# Revit family: Building-ConnessioniIEC309-GEWISS-67IB-PRESE-INTERBLOCCATE_IP67_SENZA_FONDO
name_source: partatom
category: Apparecchi elettrici
units: mm (PartAtom-declared; Revit-internal decimal feet)

## family parameters
Condiviso = Sì
Host = Superficie
Mantenere orientamento annotazione = Sì
Punto di calcolo locali = Sì
Quota connettore circolare = Usa diametro
Taglio con vuoti quando caricato = Sì
Tipo di parte = Normale

## types (23) — shared parameters
Catalogo = BUILDING
Catalogo Serie = 67 IB
Codice Electrocod = 2222
Con fondo = No
Corpo presa = GEWISS -BLU
Frequenza = 50/60 Hz
Frequenza nominale (Hz) = 50/60 Hz
Glow Wire Test = 850 °C
Glow wire test: = 850 °C
Grado di protezione = IP67
IDF = 83dda967-4c3d-4226-aae9-dec1695c669e
IDT = c02ff193-3075-4b5a-ac4b-08e79c84e21a
Immagine tipo = C.jpg
Produttore = GEWISS S.p.A.
Prospetto di default = 1219 mm
Protezione = NO (SBF)
Resistenza agli urti = IK08
SEO = Presa
Scheda Tecnica = https://www.gewiss.com
Simbolo presa = PRESAINDSTAGNA : 3P
Struttura = Grigio RAL - 7035
Temperatura di funzionamento = -25 ÷ +40 °C
Temperatura di utilizzo = -25 +40 °C
Termopressione con biglia = 125 °C
Tipologia = Verticale
URL = https://www.gewiss.com
Versione file RFA = 21.4
presa = rosso
zero-valued in all types: giallo

## per-type parameters (varying)
| type | Codice EAN | Colore | Colore: | Corrente nominale (A) | Corrente nominale (In) | Descrizione | Modello | N. poli | Numero di poli | Riferimento h | Tensione nominale | Tensione nominale: |
| GW66310N - PR.BL IP67 S.F.3P+T 16A 500V 7H SBF | 8011564741652 | Nero | Nero | 16 | 16 | PR.BL IP67 S.F.3P+T 16A 500V 7H SBF | GW66310N | 3P+T | 3P+T | 7 | 480 - 500 V | 480 - 500 V |
| GW66357N - PR.BL IP67 S.F.3P+T 32A 380V 3H SBF | 8011564742116 | Rosso | Rosso | 32 | 32 | PR.BL IP67 S.F.3P+T 32A 380V 3H SBF | GW66357N | 3P+T | 3P+T | 3 | 380 - 440 V | 380 - 440 V |
| GW66314N - PR.BL IP67 S.F.3P+N+T 32A 110V 4H SBF | 8011564741690 | Giallo | Giallo | 32 | 32 | PR.BL IP67 S.F.3P+N+T 32A 110V 4H SBF | GW66314N | 3P+N+T | 3P+N+T | 4 | 100 - 130 V | 100 - 130 V |
| GW66302N - PR.BL IP67 S.F.3P+T 16A 110V 4H SBF | 8011564741577 | Giallo | Giallo | 16 | 16 | PR.BL IP67 S.F.3P+T 16A 110V 4H SBF | GW66302N | 3P+T | 3P+T | 4 | 100 - 130 V | 100 - 130 V |
| GW66305N - PR.BL IP67 S.F.3P+T 16A 230V 9H SBF | 8011564741607 | Blu | Blu | 16 | 16 | PR.BL IP67 S.F.3P+T 16A 230V 9H SBF | GW66305N | 3P+T | 3P+T | 9 | 200 - 250 V | 200 - 250 V |
| GW66315N - PR.BL IP67 S.F.2P+T 32A 230V 6H SBF | 8011564741706 | Blu | Blu | 32 | 32 | PR.BL IP67 S.F.2P+T 32A 230V 6H SBF | GW66315N | 2P+T | 2P+T | 6 | 200 - 250 V | 200 - 250 V |
| GW66312N - PR.BL IP67 S.F.2P+T 32A 110V 4H SBF | 8011564741676 | Giallo | Giallo | 32 | 32 | PR.BL IP67 S.F.2P+T 32A 110V 4H SBF | GW66312N | 2P+T | 2P+T | 4 | 100 - 130 V | 100 - 130 V |
| GW66301N - PR.BL IP67 S.F.2P+T 16A 110V 4H SBF | 8011564741560 | Giallo | Giallo | 16 | 16 | PR.BL IP67 S.F.2P+T 16A 110V 4H SBF | GW66301N | 2P+T | 2P+T | 4 | 100 - 130 V | 100 - 130 V |
| GW66311N - PR.BL IP67 S.F.3P+N+T 16A 500V 7H SBF | 8011564741669 | Nero | Nero | 16 | 16 | PR.BL IP67 S.F.3P+N+T 16A 500V 7H SBF | GW66311N | 3P+N+T | 3P+N+T | 7 | 480 - 500 V | 480 - 500 V |
| GW66320N - PR.BL IP67 S.F.3P+N+T 32A 400V 6H SBF | 8011564741751 | Rosso | Rosso | 32 | 32 | PR.BL IP67 S.F.3P+N+T 32A 400V 6H SBF | GW66320N | 3P+N+T | 3P+N+T | 6 | 380 - 415 V | 380 - 415 V |
| GW66318N - PR.BL IP67 S.F.2P+T 32A 400V 9H SBF | 8011564741737 | Rosso | Rosso | 32 | 32 | PR.BL IP67 S.F.2P+T 32A 400V 9H SBF | GW66318N | 2P+T | 2P+T | 9 | 380 - 415 V | 380 - 415 V |
| GW66306N - PR.BL IP67 S.F.3P+N+T 16A 230V 9H SBF | 8011564741614 | Blu | Blu | 16 | 16 | PR.BL IP67 S.F.3P+N+T 16A 230V 9H SBF | GW66306N | 3P+N+T | 3P+N+T | 9 | 200 - 250 V | 200 - 250 V |
| GW66309N - PR.BL IP67 S.F.3P+N+T 16A 400V 6H SBF | 8011564741645 | Rosso | Rosso | 16 | 16 | PR.BL IP67 S.F.3P+N+T 16A 400V 6H SBF | GW66309N | 3P+N+T | 3P+N+T | 6 | 380 - 415 V | 380 - 415 V |
| GW66313N - PR.BL IP67 S.F.3P+T 32A 110V 4H SBF | 8011564741683 | Giallo | Giallo | 32 | 32 | PR.BL IP67 S.F.3P+T 32A 110V 4H SBF | GW66313N | 3P+T | 3P+T | 4 | 100 - 130 V | 100 - 130 V |
| GW66304N - PR.BL IP67 S.F.2P+T 16A 230V 6H SBF | 8011564741591 | Blu | Blu | 16 | 16 | PR.BL IP67 S.F.2P+T 16A 230V 6H SBF | GW66304N | 2P+T | 2P+T | 6 | 200 - 250 V | 200 - 250 V |
| GW66321N - PR.BL IP67 S.F.3P+T 32A 500V 7H SBF | 8011564741768 | Nero | Nero | 32 | 32 | PR.BL IP67 S.F.3P+T 32A 500V 7H SBF | GW66321N | 3P+T | 3P+T | 7 | 480 - 500 V | 480 - 500 V |
| GW66316N - PR.BL IP67 S.F.3P+T 32A 230V 9H SBF | 8011564741713 | Blu | Blu | 32 | 32 | PR.BL IP67 S.F.3P+T 32A 230V 9H SBF | GW66316N | 3P+T | 3P+T | 9 | 200 - 250 V | 200 - 250 V |
| GW66322N - PR.BL IP67 S.F.3P+N+T 32A 500V 7H SBF | 8011564741775 | Nero | Nero | 32 | 32 | PR.BL IP67 S.F.3P+N+T 32A 500V 7H SBF | GW66322N | 3P+N+T | 3P+N+T | 7 | 480 - 500 V | 480 - 500 V |
| GW66319N - PR.BL IP67 S.F.3P+T 32A 400V 6H SBF | 8011564741744 | Rosso | Rosso | 32 | 32 | PR.BL IP67 S.F.3P+T 32A 400V 6H SBF | GW66319N | 3P+T | 3P+T | 6 | 380 - 415 V | 380 - 415 V |
| GW66317N - PR.BL IP67 S.F.3P+N+T 32A 230V 9H SBF | 8011564741720 | Blu | Blu | 32 | 32 | PR.BL IP67 S.F.3P+N+T 32A 230V 9H SBF | GW66317N | 3P+N+T | 3P+N+T | 9 | 200 - 250 V | 200 - 250 V |
| GW66308N - PR.BL IP67 S.F.3P+T 16A 400V 6H SBF | 8011564741638 | Rosso | Rosso | 16 | 16 | PR.BL IP67 S.F.3P+T 16A 400V 6H SBF | GW66308N | 3P+T | 3P+T | 6 | 380 - 415 V | 380 - 415 V |
| GW66303N - PR.BL IP67 S.F.3P+N+T 16A 110V 4H SBF | 8011564741584 | Giallo | Giallo | 16 | 16 | PR.BL IP67 S.F.3P+N+T 16A 110V 4H SBF | GW66303N | 3P+N+T | 3P+N+T | 4 | 100 - 130 V | 100 - 130 V |
| GW66307N - PR.BL IP67 S.F.2P+T 16A 400V 9H SBF | 8011564741621 | Rosso | Rosso | 16 | 16 | PR.BL IP67 S.F.2P+T 16A 400V 9H SBF | GW66307N | 2P+T | 2P+T | 9 | 380 - 415 V | 380 - 415 V |

## geometry (parser evidence)
native form markers: Sweep x4
no freeform markers — native parametric forms only
